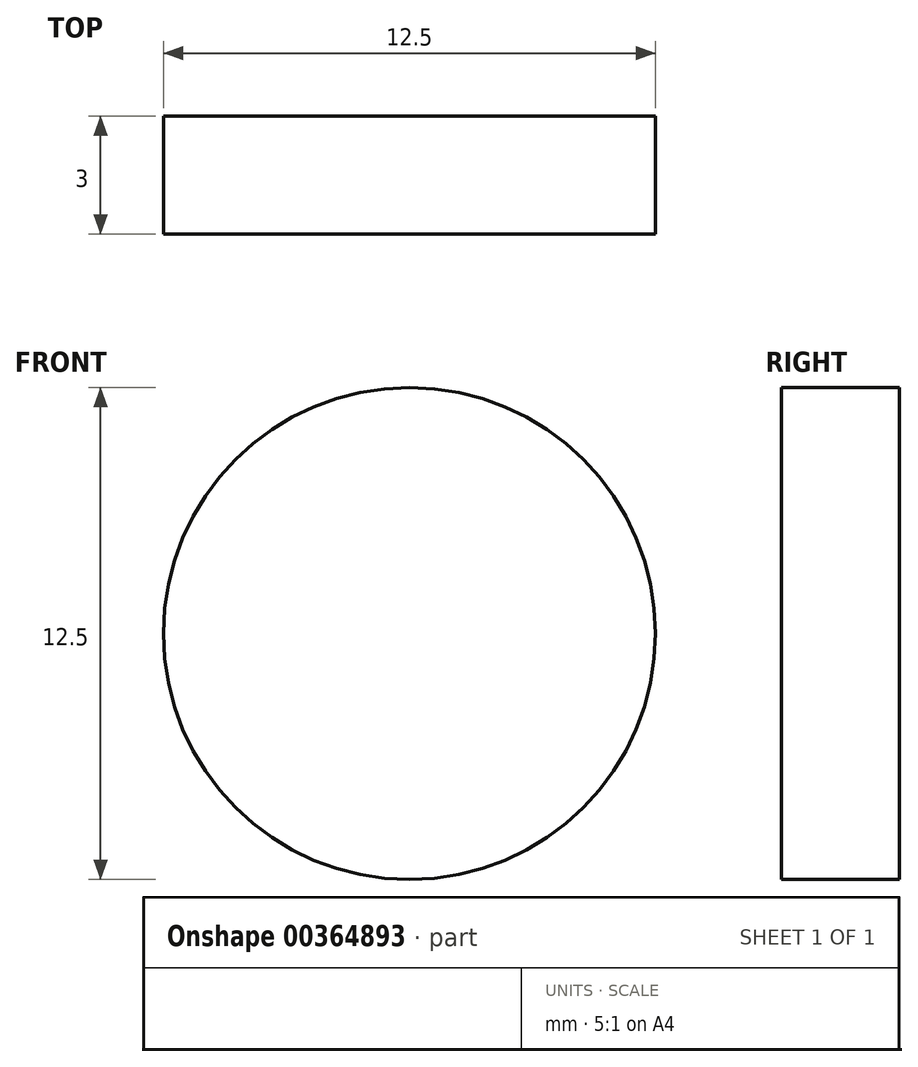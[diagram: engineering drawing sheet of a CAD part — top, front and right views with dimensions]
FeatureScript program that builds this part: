
annotation { "Feature Type Name" : "Feature", "Feature Type Description" : "" }
export const myFeature = defineFeature(function(context is Context, id is Id, definition is map)
    precondition{}
    {
        {
            var Q0;
            Q0=qCreatedBy(makeId("Front.planeOp"),FACE);
            var sketch = newSketch(context, id + "F0", { "sketchPlane" : qUnion([Q0])});
            skCircle(sketch, "E0", {"center": v(0, 0) * mm, "radius": 6.25 * mm});
            skSolve(sketch);
        }
        {
            var Q0;
            Q0=makeQuery(id+"F0.imprint","IMPRINT",FACE,{"disambiguationData":[TD([[makeQuery(id+"F0.imprint","IMPRINT",EDGE,{"derivedFrom":sQuery(id+"F0.wireOp",EDGE,"E0")}),1.0]])]});
            extrude(context, id + "F1", {"entities" : qUnion([Q0]), "depth" : 3 * mm});
        }
    });
